# Revit family: LHBT
name_source: partatom
category: Lighting Fixtures
units: mm (PartAtom-declared; Revit-internal decimal feet)

## family parameters
Always vertical = Yes
Cut with Voids When Loaded = No
Host = Ceiling
Light Source = Yes
OmniClass Number = 23.80.70.11.14.17
OmniClass Title = Direct/Indirect
Part Type = Normal
Room Calculation Point = No
Round Connector Dimension = Use Diameter
Shared = No

## types (16) — shared parameters
Assembly Code = D5020200
Color Filter = 16777215
Description = LED High Bay T-Bar Grid
Dimming Lamp Color Temperature Shift = <None>
Emit Shape Visible in Rendering = No
Emit from Rectangle Width = 1' - 11 11/16"
Height = 0' - 3 1/2"
Housing Finish = Metal - Viscor - White
Lamp = LED
Manufacturer = VISIONEERING by VISCOR
Model = LHBT
Tilt Angle = 90.00°
URL = https://www.viscor.com
Voltage = 120 V
Width = 1' - 11 11/16"

## per-type parameters (varying)
| type | Apparent Load | Emit from Rectangle Length | Lamp Wattage | Length | Lens Finish | Lens Not Shown | Lens Shown | Open Lens | Photometric Web File |
| LHBT2x4-LED840K120LUNV-P73 | 78 VA | 3' - 11 3/4" | 78 VA | 3' - 11 3/4" | Polycarbonate - Viscor - White Translucent Lay-In Lens | No | Yes | <By Category> | LHBT2X4-LED840K120LUNV-P73.ies |
| LHBT2x2-LED840K080LUNV-P73 | 49 VA | 1' - 11 3/4" | 49 VA | 1' - 11 3/4" | Polycarbonate - Viscor - White Translucent Lay-In Lens | No | Yes | <By Category> | LHBT2X2-LED840K080LUNV-P73.ies |
| LHBT2x4-LED840K150LUNV-P73 | 98 VA | 3' - 11 3/4" | 98 VA | 3' - 11 3/4" | Polycarbonate - Viscor - White Translucent Lay-In Lens | No | Yes | <By Category> | LHBT2X4-LED840K150LUNV-P73.ies |
| LHBT2x4-LED840K180LUNV-P73 | 118 VA | 3' - 11 3/4" | 118 VA | 3' - 11 3/4" | Polycarbonate - Viscor - White Translucent Lay-In Lens | No | Yes | <By Category> | LHBT2X4-LED840K180LUNV-P73.ies |
| LHBT2x4-LED840K240LUNV-P73 | 162 VA | 3' - 11 3/4" | 162 VA | 3' - 11 3/4" | Polycarbonate - Viscor - White Translucent Lay-In Lens | No | Yes | <By Category> | LHBT2X4-LED840K240LUNV-P73.ies |
| LHBT2x4-LED840K300LUNV-P73 | 205 VA | 3' - 11 3/4" | 205 VA | 3' - 11 3/4" | Polycarbonate - Viscor - White Translucent Lay-In Lens | No | Yes | <By Category> | LHBT2X4-LED840K300LUNV-P73.ies |
| LHBT2x2-LED840K120LUNV-P73 | 81 VA | 1' - 11 3/4" | 81 VA | 1' - 11 3/4" | Polycarbonate - Viscor - White Translucent Lay-In Lens | No | Yes | <By Category> | LHBT2X2-LED840K120LUNV-P73.ies |
| LHBT2x2-LED840K150LUNV-P73 | 102 VA | 1' - 11 3/4" | 102 VA | 1' - 11 3/4" | Polycarbonate - Viscor - White Translucent Lay-In Lens | No | Yes | <By Category> | LHBT2X2-LED840K150LUNV-P73.ies |
| LHBT2X2-LED840K080LUNV | 49 VA | 1' - 11 3/4" | 49 VA | 1' - 11 3/4" | <By Category> | Yes | No | No Lens | LHBT2X2-LED840K080LUNV.ies |
| LHBT2X2-LED840K120LUNV | 81 VA | 1' - 11 3/4" | 81 VA | 1' - 11 3/4" | <By Category> | Yes | No | <By Category> | LHBT2X2-LED840K120LUNV.ies |
| LHBT2X2-LED840K150LUNV | 102 VA | 1' - 11 3/4" | 102 VA | 1' - 11 3/4" | <By Category> | Yes | No | <By Category> | LHBT2X2-LED840K150LUNV.ies |
| LHBT2X4-LED840K120LUNV | 78 VA | 3' - 11 3/4" | 78 VA | 3' - 11 3/4" | <By Category> | Yes | No | <By Category> | LHBT2X4-LED840K120LUNV.ies |
| LHBT2X4-LED840K150LUNV | 98 VA | 3' - 11 3/4" | 98 VA | 3' - 11 3/4" | <By Category> | Yes | No | <By Category> | LHBT2X4-LED840K150LUNV.ies |
| LHBT2X4-LED840K180LUNV | 118 VA | 3' - 11 3/4" | 118 VA | 3' - 11 3/4" | <By Category> | Yes | No | <By Category> | LHBT2X4-LED840K180LUNV.ies |
| LHBT2X4-LED840K240LUNV | 162 VA | 3' - 11 3/4" | 162 VA | 3' - 11 3/4" | <By Category> | Yes | No | <By Category> | LHBT2X4-LED840K240LUNV.ies |
| LHBT2X4-LED840K300LUNV | 205 VA | 3' - 11 3/4" | 205 VA | 3' - 11 3/4" | <By Category> | Yes | No | <By Category> | LHBT2X4-LED840K300LUNV.ies |

## geometry (parser evidence)
native form markers: Sweep x2
no freeform markers — native parametric forms only
